# Revit family: Lay-In Ceiling Heaters
name_source: partatom
category: Mechanical Equipment
revit_build: Autodesk Revit 2017 (Build: 20171027_0315(x64)
units: mm (PartAtom-declared; Revit-internal decimal feet)

## family parameters
Always vertical = No
Cut with Voids When Loaded = No
Host = Ceiling
OmniClass Number = 23.75.00.00
OmniClass Title = Climate Control (HVAC)
Part Type = Normal
Room Calculation Point = No
Round Connector Dimension = Use Diameter
Shared = No

## types (12) — shared parameters
Apparent Load = 0 VA
Frequency = 0 Hz
Height 1 = 0' - 1 1/2"
Height 2 = 0' - 3"
Manufacturer = CeramicCircuit Infrared Radiant Heaters
Modeled By = Smith LaRock Architecture | www.slarc.com
Mounting Depth = 0' - 0"
Number of Poles = 1
Phase = 1
Product Documentation Link = http://192.185.145.162
Product Name = LAY-IN CEILING HEATER
Product Page URL = http://electricheat.com
Recess Mount = No
Semi Recess Mount = No
Surface Mount = Yes
Total Heating Capacity = 2134 Btu/s
URL = http://electricheat.com
zero-valued in all types: Power Factor

## per-type parameters (varying)
| type | Amps | Frame | Length | Panel | Voltage | Watts | Width |
| 1624CL - 120V | 5 A | <By Category> | 2' - 0" | <By Category> | 120 V | 625 W | 2' - 0" |
| 1624CL - 208V | 3 A | <By Category> | 2' - 0" | <By Category> | 208 V | 625 W | 2' - 0" |
| 1624CL - 240V | 3 A | <By Category> | 2' - 0" | <By Category> | 240 V | 625 W | 2' - 0" |
| 1624CL - 277V | 2 A | Default | 2' - 0" | Default | 277 V | 625 W | 2' - 0" |
| 1648CL - 277V | 5 A | Default | 4' - 0" | Default | 277 V | 1250 W | 2' - 0" |
| 1648CL - 120V | 10 A | Default | 4' - 0" | Default | 120 V | 1250 W | 2' - 0" |
| 1648CL - 208V | 6 A | Default | 4' - 0" | Default | 208 V | 1250 W | 2' - 0" |
| 1648CL - 240V | 5 A | Default | 4' - 0" | Default | 240 V | 1250 W | 2' - 0" |
| 1248CL - 277V | 3 A | Default | 4' - 0" | Default | 277 V | 750 W | 1' - 0" |
| 1248CL - 120V | 6 A | Default | 4' - 0" | Default | 120 V | 750 W | 1' - 0" |
| 1248CL - 208V | 4 A | Default | 4' - 0" | Default | 208 V | 750 W | 1' - 0" |
| 1248CL - 240V | 3 A | Default | 4' - 0" | Default | 240 V | 750 W | 1' - 0" |

## geometry (parser evidence)
native form markers: Sweep x4
no freeform markers — native parametric forms only
